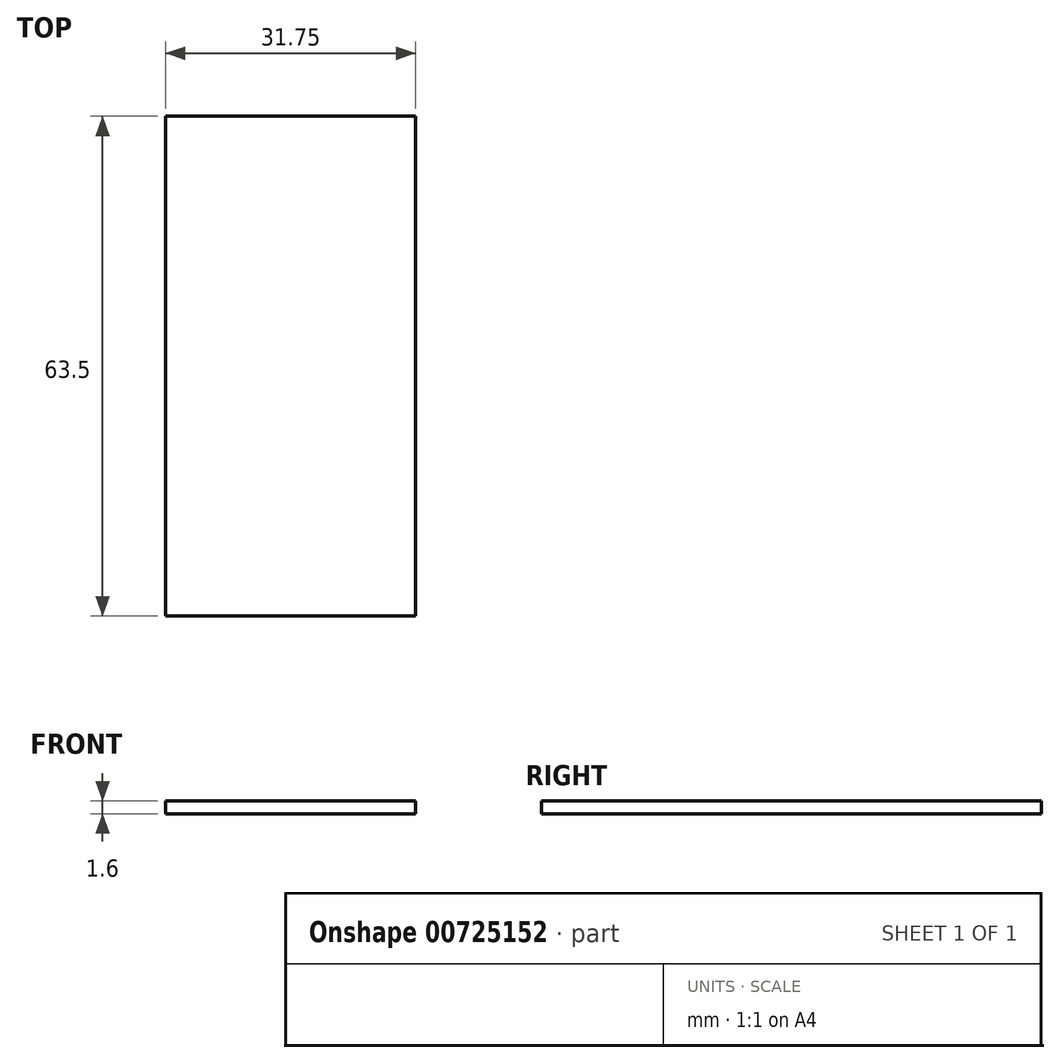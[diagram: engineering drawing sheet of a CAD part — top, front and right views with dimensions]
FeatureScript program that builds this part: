
annotation { "Feature Type Name" : "Feature", "Feature Type Description" : "" }
export const myFeature = defineFeature(function(context is Context, id is Id, definition is map)
    precondition{}
    {
        {
            var Q0;
            Q0=qCreatedBy(makeId("Top.planeOp"),FACE);
            var sketch = newSketch(context, id + "F0", { "sketchPlane" : qUnion([Q0])});
            skLineSegment(sketch, "E0.bottom", {"start": v(-143.78, -54.79) * mm, "end": v(-112.03, -54.79) * mm});
            skLineSegment(sketch, "E0.top", {"start": v(-143.78, 8.71) * mm, "end": v(-112.03, 8.71) * mm});
            skLineSegment(sketch, "E0.left", {"start": v(-143.78, -54.79) * mm, "end": v(-143.78, 8.71) * mm});
            skLineSegment(sketch, "E0.right", {"start": v(-112.03, -54.79) * mm, "end": v(-112.03, 8.71) * mm});
            skSolve(sketch);
        }
        {
            var Q0;
            Q0=makeQuery(id+"F0.imprint","IMPRINT",FACE,{"disambiguationData":[TD([[makeQuery(id+"F0.imprint","IMPRINT",EDGE,{"derivedFrom":sQuery(id+"F0.wireOp",EDGE,"E0.bottom")}),1.0]])]});
            extrude(context, id + "F1", {"entities" : qUnion([Q0]), "depth" : 1.6 * mm, "offsetDistance" : 25.4 * mm});
        }
    });
